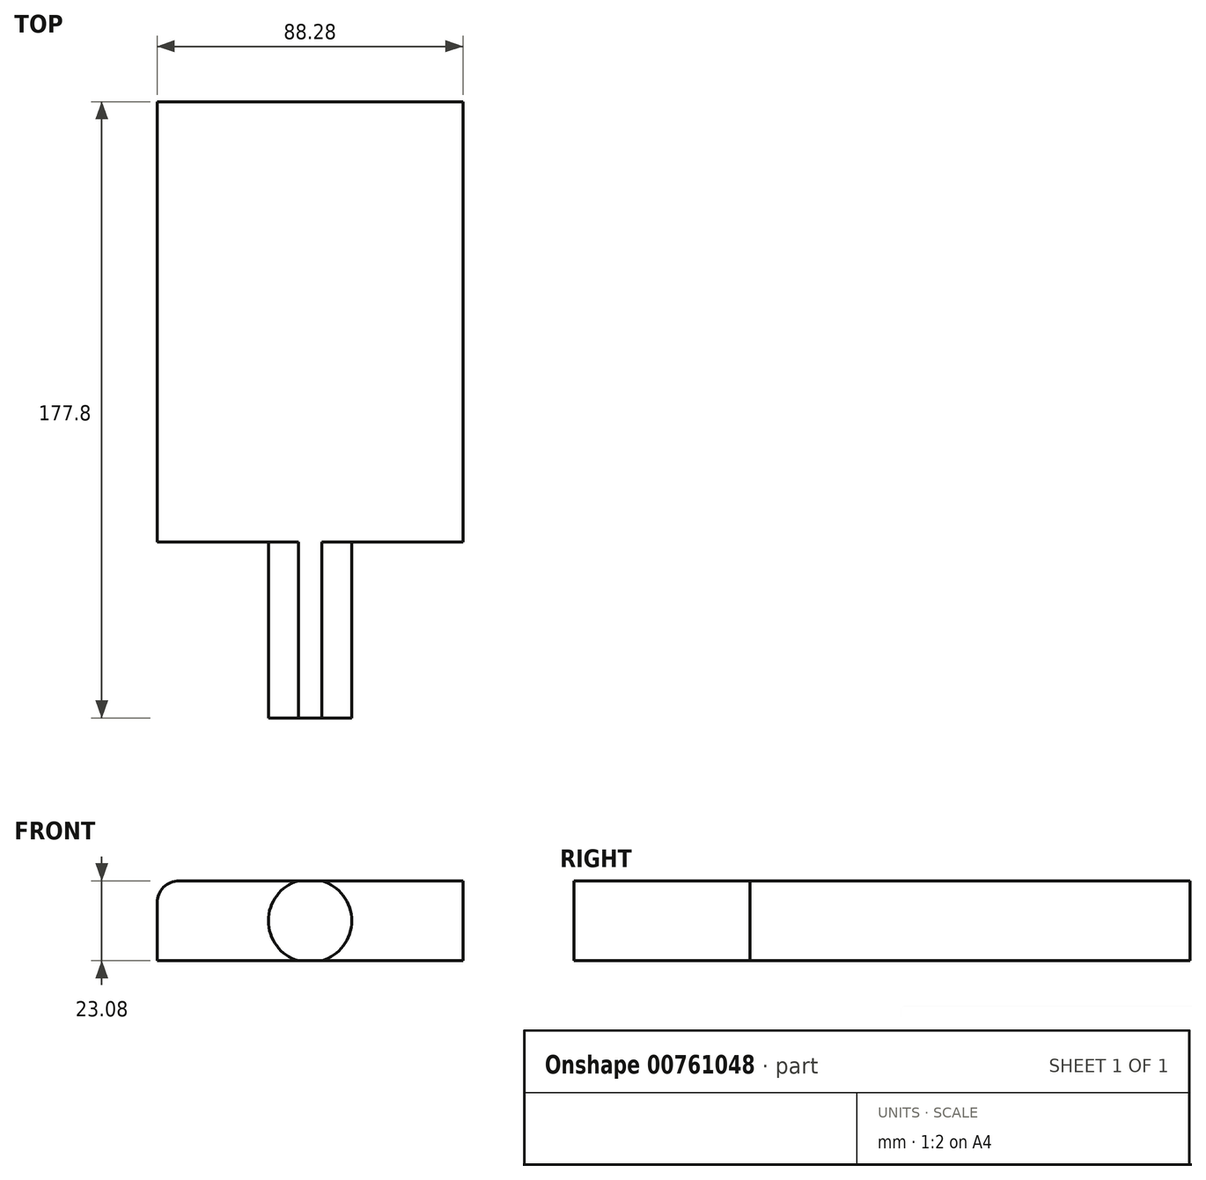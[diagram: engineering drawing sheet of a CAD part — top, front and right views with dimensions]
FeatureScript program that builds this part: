
annotation { "Feature Type Name" : "Feature", "Feature Type Description" : "" }
export const myFeature = defineFeature(function(context is Context, id is Id, definition is map)
    precondition{}
    {
        {
            var Q0;
            Q0=qCreatedBy(makeId("Front.planeOp"),FACE);
            var sketch = newSketch(context, id + "F0", { "sketchPlane" : qUnion([Q0])});
            skPoint(sketch, "E0", {"position": v(18.25, 45.85) * mm});
            skPoint(sketch, "E1", {"position": v(18.25, 17.78) * mm});
            skLineSegment(sketch, "E2.bottom", {"start": v(44.14, -11.54) * mm, "end": v(-44.14, -11.54) * mm});
            skLineSegment(sketch, "E2.top", {"start": v(44.14, 11.54) * mm, "end": v(-37.79, 11.54) * mm});
            skLineSegment(sketch, "E2.left", {"start": v(44.14, -11.54) * mm, "end": v(44.14, 11.54) * mm});
            skLineSegment(sketch, "E2.right", {"start": v(-44.14, -11.54) * mm, "end": v(-44.14, 5.2) * mm});
            skPoint(sketch, "E2.middle", {"position": v(0, 0) * mm});
            skPoint(sketch, "E3.visualSharp", {"position": v(-44.14, 11.54) * mm});
            skArc(sketch, "E3.filletArc", {"start": v(-37.79, 11.54) * mm, "mid": v(-42.28, 9.68) * mm, "end": v(-44.14, 5.2) * mm});
            skSolve(sketch);
        }
        {
            var Q0;
            Q0=makeQuery(id+"F0.imprint","IMPRINT",FACE,{"disambiguationData":[TD([[makeQuery(id+"F0.imprint","IMPRINT",EDGE,{"derivedFrom":sQuery(id+"F0.wireOp",EDGE,"E2.bottom")}),-1.0]])]});
            extrude(context, id + "F1", {"entities" : qUnion([Q0]), "oppositeDirection" : true, "depth" : 127 * mm, "offsetDistance" : 25.4 * mm});
        }
        {
            var Q0;
            Q0=makeQuery(id+"F1.opExtrude","CAP_FACE",FACE,{"disambiguationData":[OSD([sQuery(id+"F0.wireOp",EDGE,"E2.bottom"),sQuery(id+"F0.wireOp",EDGE,"E2.top"),sQuery(id+"F0.wireOp",EDGE,"E2.left"),sQuery(id+"F0.wireOp",EDGE,"E2.right"),sQuery(id+"F0.wireOp",EDGE,"E3.filletArc")])],"isStart":true});
            var sketch = newSketch(context, id + "F2", { "sketchPlane" : qUnion([Q0])});
            skCircle(sketch, "E4", {"center": v(0, 0) * mm, "radius": 12.02 * mm});
            skCircle(sketch, "E5", {"center": v(0, 0) * mm, "radius": 7.65 * mm});
            skSolve(sketch);
        }
        {
            var Q0;
            Q0=makeQuery(id+"F2.imprint","IMPRINT",FACE,{"disambiguationData":[TD([[makeQuery(id+"F2.imprint","IMPRINT",EDGE,{"derivedFrom":sQuery(id+"F2.wireOp",EDGE,"E5")}),-1.0]])]});
            var Q1;
            Q1=makeQuery(id+"F2.imprint","IMPRINT",FACE,{"disambiguationData":[TD([[makeQuery(id+"F2.imprint","IMPRINT",EDGE,{"derivedFrom":sQuery(id+"F2.wireOp",EDGE,"E5")}),1.0]])]});
            var Q2;
            {var subQ0=sQuery(id+"F2.wireOp",EDGE,"E4");var subQ1=makeQuery(id+"F1.opExtrude","CAP_EDGE",EDGE,{"disambiguationData":[OSD([sQuery(id+"F0.wireOp",EDGE,"E2.top")])],"isStart":true});var subQ2=makeQuery(id+"F2.imprint","INTERSECT",VERTEX,{"disambiguationData":[OD(0.0)],"derivedFrom":[subQ1,subQ0]});Q2=makeQuery(id+"F2.imprint","IMPRINT",FACE,{"disambiguationData":[TD([[makeQuery(id+"F2.imprint","IMPRINT",EDGE,{"disambiguationData":[TD([[subQ2,1.0]])],"derivedFrom":subQ0}),1.0]])]});}
            var Q3;
            {var subQ0=sQuery(id+"F2.wireOp",EDGE,"E4");var subQ1=makeQuery(id+"F1.opExtrude","CAP_EDGE",EDGE,{"disambiguationData":[OSD([sQuery(id+"F0.wireOp",EDGE,"E2.bottom")])],"isStart":true});var subQ2=makeQuery(id+"F2.imprint","INTERSECT",VERTEX,{"disambiguationData":[OD(0.0)],"derivedFrom":[subQ1,subQ0]});Q3=makeQuery(id+"F2.imprint","IMPRINT",FACE,{"disambiguationData":[TD([[makeQuery(id+"F2.imprint","IMPRINT",EDGE,{"disambiguationData":[TD([[subQ2,-1.0]])],"derivedFrom":subQ0}),1.0]])]});}
            extrude(context, id + "F3", {"entities" : qUnion([Q0, Q1, Q2, Q3]), "operationType" : NewBodyOperationType.ADD, "depth" : 50.8 * mm, "offsetDistance" : 25.4 * mm});
        }
    });
